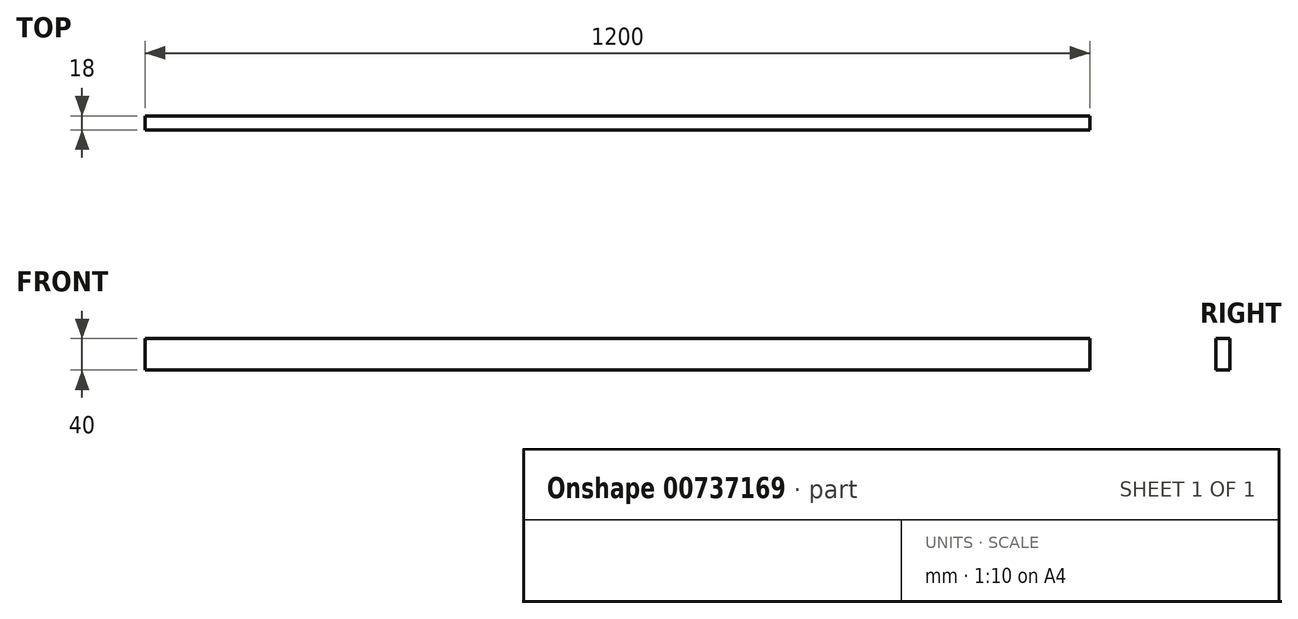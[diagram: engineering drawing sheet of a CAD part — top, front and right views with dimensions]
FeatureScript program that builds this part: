
annotation { "Feature Type Name" : "Feature", "Feature Type Description" : "" }
export const myFeature = defineFeature(function(context is Context, id is Id, definition is map)
    precondition{}
    {
        {
            var Q0;
            Q0=qCreatedBy(makeId("Front.planeOp"),FACE);
            var sketch = newSketch(context, id + "F0", { "sketchPlane" : qUnion([Q0])});
            skLineSegment(sketch, "E0.bottom", {"start": v(600, 20) * mm, "end": v(-600, 20) * mm});
            skLineSegment(sketch, "E0.top", {"start": v(600, -20) * mm, "end": v(-600, -20) * mm});
            skLineSegment(sketch, "E0.left", {"start": v(600, 20) * mm, "end": v(600, -20) * mm});
            skLineSegment(sketch, "E0.right", {"start": v(-600, 20) * mm, "end": v(-600, -20) * mm});
            skPoint(sketch, "E0.middle", {"position": v(0, 0) * mm});
            skSolve(sketch);
        }
        {
            var Q0;
            Q0 = qSketchRegion(id + "F0", true);
            extrude(context, id + "F1", {"entities" : qUnion([Q0]), "depth" : 18 * mm, "offsetDistance" : 25 * mm});
        }
    });
